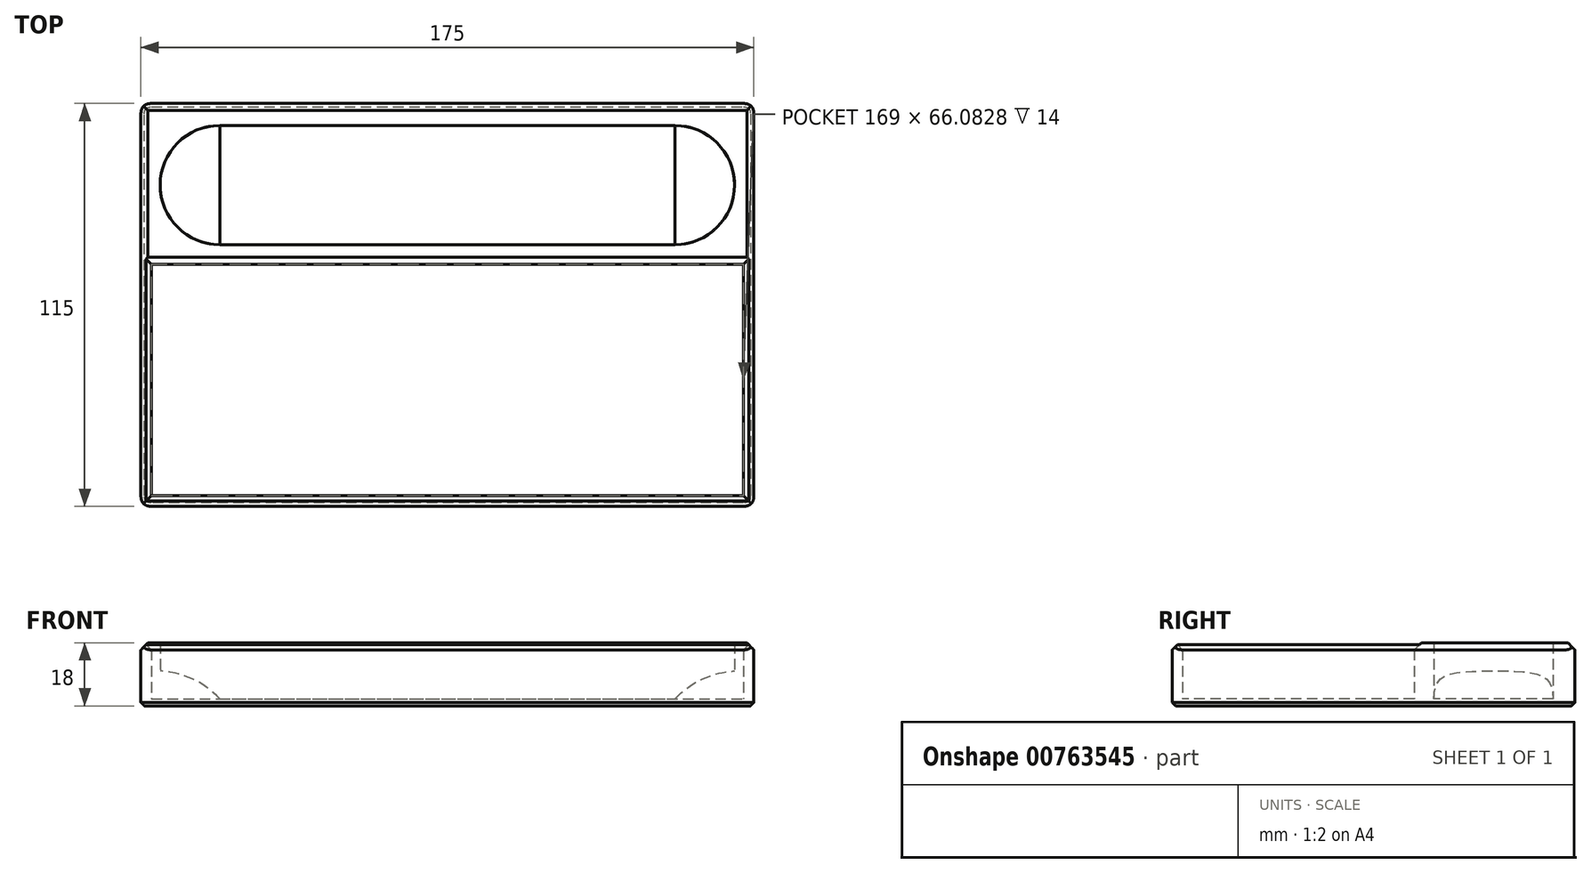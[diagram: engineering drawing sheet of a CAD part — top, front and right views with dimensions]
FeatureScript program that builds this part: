
annotation { "Feature Type Name" : "Feature", "Feature Type Description" : "" }
export const myFeature = defineFeature(function(context is Context, id is Id, definition is map)
    precondition{}
    {
        {
            var Q0;
            Q0=qCreatedBy(makeId("Top.planeOp"),FACE);
            var sketch = newSketch(context, id + "F0", { "sketchPlane" : qUnion([Q0])});
            skLineSegment(sketch, "E0.bottom", {"start": v(-100.46, 59.85) * mm, "end": v(74.54, 59.85) * mm});
            skLineSegment(sketch, "E0.top", {"start": v(-100.46, -55.15) * mm, "end": v(74.54, -55.15) * mm});
            skLineSegment(sketch, "E0.left", {"start": v(-100.46, 59.85) * mm, "end": v(-100.46, -55.15) * mm});
            skLineSegment(sketch, "E0.right", {"start": v(74.54, 59.85) * mm, "end": v(74.54, -55.15) * mm});
            skLineSegment(sketch, "E1.bottom", {"start": v(-77.96, 53.55) * mm, "end": v(52.04, 53.55) * mm});
            skLineSegment(sketch, "E1.top", {"start": v(-77.96, 19.55) * mm, "end": v(52.04, 19.55) * mm});
            skLineSegment(sketch, "E2.bottom", {"start": v(-97.46, 13.93) * mm, "end": v(71.54, 13.93) * mm});
            skLineSegment(sketch, "E2.top", {"start": v(-97.46, -52.15) * mm, "end": v(71.54, -52.15) * mm});
            skLineSegment(sketch, "E2.left", {"start": v(-97.46, 13.93) * mm, "end": v(-97.46, -52.15) * mm});
            skLineSegment(sketch, "E2.right", {"start": v(71.54, 13.93) * mm, "end": v(71.54, -52.15) * mm});
            skLineSegment(sketch, "E3", {"start": v(-97.46, -6.12) * mm, "end": v(-100.46, -6.12) * mm, "construction": true});
            skLineSegment(sketch, "E4", {"start": v(71.54, 0) * mm, "end": v(74.54, 0) * mm, "construction": true});
            skLineSegment(sketch, "E5", {"start": v(-2.83, -52.15) * mm, "end": v(-2.83, -55.15) * mm, "construction": true});
            skArc(sketch, "E6", {"start": v(-77.96, 53.55) * mm, "mid": v(-94.96, 36.55) * mm, "end": v(-77.96, 19.55) * mm});
            skPoint(sketch, "E6.third.point", {"position": v(-94.96, 36.55) * mm});
            skLineSegment(sketch, "E7", {"start": v(-94.96, 36.55) * mm, "end": v(-100.46, 36.55) * mm, "construction": true});
            skArc(sketch, "E8", {"start": v(52.04, 19.55) * mm, "mid": v(69.04, 36.55) * mm, "end": v(52.04, 53.55) * mm});
            skLineSegment(sketch, "E9", {"start": v(74.54, 36.55) * mm, "end": v(69.04, 36.55) * mm, "construction": true});
            skLineSegment(sketch, "E10", {"start": v(-77.96, 53.55) * mm, "end": v(-77.96, 19.55) * mm});
            skLineSegment(sketch, "E11", {"start": v(52.04, 53.55) * mm, "end": v(52.04, 19.55) * mm});
            skSolve(sketch);
        }
        {
            var Q0;
            Q0=makeQuery(id+"F0.imprint","IMPRINT",FACE,{"disambiguationData":[TD([[makeQuery(id+"F0.imprint","IMPRINT",EDGE,{"derivedFrom":sQuery(id+"F0.wireOp",EDGE,"E0.bottom")}),-1.0]])]});
            extrude(context, id + "F1", {"entities" : qUnion([Q0]), "depth" : 18 * mm, "offsetDistance" : 25 * mm});
        }
        {
            var Q0;
            Q0=makeQuery(id+"F0.imprint","IMPRINT",FACE,{"disambiguationData":[TD([[makeQuery(id+"F0.imprint","IMPRINT",EDGE,{"derivedFrom":sQuery(id+"F0.wireOp",EDGE,"E1.bottom")}),-1.0]])]});
            var Q1;
            Q1=makeQuery(id+"F0.imprint","IMPRINT",FACE,{"disambiguationData":[TD([[makeQuery(id+"F0.imprint","IMPRINT",EDGE,{"derivedFrom":sQuery(id+"F0.wireOp",EDGE,"E2.bottom")}),-1.0]])]});
            extrude(context, id + "F2", {"entities" : qUnion([Q0, Q1]), "operationType" : NewBodyOperationType.ADD, "depth" : 2 * mm, "offsetDistance" : 25 * mm});
        }
        {
            var Q0;
            Q0=makeQuery(id+"F0.imprint","IMPRINT",FACE,{"disambiguationData":[TD([[makeQuery(id+"F0.imprint","IMPRINT",EDGE,{"derivedFrom":sQuery(id+"F0.wireOp",EDGE,"E6")}),1.0]])]});
            var Q1;
            Q1=makeQuery(id+"F0.imprint","IMPRINT",FACE,{"disambiguationData":[TD([[makeQuery(id+"F0.imprint","IMPRINT",EDGE,{"derivedFrom":sQuery(id+"F0.wireOp",EDGE,"E8")}),1.0]])]});
            extrude(context, id + "F3", {"entities" : qUnion([Q0, Q1]), "operationType" : NewBodyOperationType.ADD, "depth" : 10 * mm, "offsetDistance" : 25 * mm});
        }
        {
            var Q0;
            Q0=makeQuery(id+"F3.opExtrude","CAP_EDGE",EDGE,{"disambiguationData":[OSD([sQuery(id+"F0.wireOp",EDGE,"E10")])],"isStart":false});
            var Q1;
            Q1=makeQuery(id+"F3.opExtrude","CAP_EDGE",EDGE,{"disambiguationData":[OSD([sQuery(id+"F0.wireOp",EDGE,"E11")])],"isStart":false});
            fillet(context, id + "F4", {"entities" : qUnion([Q0, Q1]), "radius" : 24.87 * mm, "tangentPropagation" : true, "allowEdgeOverflow" : false});
        }
        {
            var Q0;
            Q0=makeQuery(id+"F1.opExtrude","CAP_EDGE",EDGE,{"disambiguationData":[OSD([sQuery(id+"F0.wireOp",EDGE,"E2.bottom")])],"isStart":false});
            var Q1;
            Q1=makeQuery(id+"F1.opExtrude","CAP_EDGE",EDGE,{"disambiguationData":[OSD([sQuery(id+"F0.wireOp",EDGE,"E2.left")])],"isStart":false});
            var Q2;
            Q2=makeQuery(id+"F1.opExtrude","CAP_EDGE",EDGE,{"disambiguationData":[OSD([sQuery(id+"F0.wireOp",EDGE,"E2.top")])],"isStart":false});
            var Q3;
            Q3=makeQuery(id+"F1.opExtrude","CAP_EDGE",EDGE,{"disambiguationData":[OSD([sQuery(id+"F0.wireOp",EDGE,"E2.right")])],"isStart":false});
            var Q4;
            Q4=makeQuery(id+"F1.opExtrude","CAP_EDGE",EDGE,{"disambiguationData":[OSD([sQuery(id+"F0.wireOp",EDGE,"E0.left")])],"isStart":false});
            var Q5;
            Q5=makeQuery(id+"F1.opExtrude","CAP_EDGE",EDGE,{"disambiguationData":[OSD([sQuery(id+"F0.wireOp",EDGE,"E0.bottom")])],"isStart":false});
            var Q6;
            Q6=makeQuery(id+"F1.opExtrude","CAP_EDGE",EDGE,{"disambiguationData":[OSD([sQuery(id+"F0.wireOp",EDGE,"E0.right")])],"isStart":false});
            var Q7;
            Q7=makeQuery(id+"F1.opExtrude","CAP_EDGE",EDGE,{"disambiguationData":[OSD([sQuery(id+"F0.wireOp",EDGE,"E0.top")])],"isStart":false});
            chamfer(context, id + "F5", {"entities" : qUnion([Q0, Q1, Q2, Q3, Q4, Q5, Q6, Q7]), "width" : 2 * mm, "tangentPropagation" : true});
        }
        {
            var Q0;
            Q0=makeQuery(id+"F1.opExtrude","SWEPT_EDGE",EDGE,{"disambiguationData":[OSD([sQuery(id+"F0.wireOp",EDGE,"E0.top"),sQuery(id+"F0.wireOp",EDGE,"E0.right")])]});
            var Q1;
            Q1=makeQuery(id+"F1.opExtrude","SWEPT_EDGE",EDGE,{"disambiguationData":[OSD([sQuery(id+"F0.wireOp",EDGE,"E0.bottom"),sQuery(id+"F0.wireOp",EDGE,"E0.right")])]});
            var Q2;
            Q2=makeQuery(id+"F1.opExtrude","SWEPT_EDGE",EDGE,{"disambiguationData":[OSD([sQuery(id+"F0.wireOp",EDGE,"E0.top"),sQuery(id+"F0.wireOp",EDGE,"E0.left")])]});
            var Q3;
            Q3=makeQuery(id+"F1.opExtrude","SWEPT_EDGE",EDGE,{"disambiguationData":[OSD([sQuery(id+"F0.wireOp",EDGE,"E0.bottom"),sQuery(id+"F0.wireOp",EDGE,"E0.left")])]});
            fillet(context, id + "F6", {"entities" : qUnion([Q0, Q1, Q2, Q3]), "radius" : 3 * mm, "tangentPropagation" : true, "rho" : 0.5, "crossSection" : FilletCrossSection.CONIC, "allowEdgeOverflow" : false});
        }
        {
            var Q0;
            Q0=makeQuery(id+"F1.opExtrude","CAP_EDGE",EDGE,{"disambiguationData":[OSD([sQuery(id+"F0.wireOp",EDGE,"E0.top")])],"isStart":true});
            var Q1;
            {var subQ0=sQuery(id+"F0.wireOp",EDGE,"E11");var subQ1=sQuery(id+"F0.wireOp",EDGE,"E8");var subQ2=sQuery(id+"F0.wireOp",EDGE,"E10");var subQ3=sQuery(id+"F0.wireOp",EDGE,"E6");var subQ4=sQuery(id+"F0.wireOp",EDGE,"E2.right");var subQ5=sQuery(id+"F0.wireOp",EDGE,"E2.left");var subQ6=sQuery(id+"F0.wireOp",EDGE,"E2.top");var subQ7=sQuery(id+"F0.wireOp",EDGE,"E2.bottom");var subQ8=sQuery(id+"F0.wireOp",EDGE,"E1.top");var subQ9=sQuery(id+"F0.wireOp",EDGE,"E1.bottom");var subQ10=sQuery(id+"F0.wireOp",EDGE,"E0.right");var subQ11=sQuery(id+"F0.wireOp",EDGE,"E0.top");Q1=makeQuery(id+"F6.opFillet","BLEND_EDGE",EDGE,{"blendedFrom":[makeQuery(id+"F1.opExtrude","SWEPT_EDGE",EDGE,{"disambiguationData":[OSD([subQ11,subQ10])]}),makeQuery(id+"F3.boolean.opBoolean","MERGE",FACE,{"derivedFrom":[makeQuery(id+"F2.boolean.opBoolean","MERGE",FACE,{"derivedFrom":[makeQuery(id+"F1.opExtrude","CAP_FACE",FACE,{"disambiguationData":[OSD([sQuery(id+"F0.wireOp",EDGE,"E0.bottom"),subQ11,sQuery(id+"F0.wireOp",EDGE,"E0.left"),subQ10,subQ9,subQ8,subQ7,subQ6,subQ5,subQ4,subQ3,subQ1])],"isStart":true}),makeQuery(id+"F2.opExtrude","CAP_FACE",FACE,{"disambiguationData":[OSD([subQ9,subQ8,subQ2,subQ0])],"isStart":true}),makeQuery(id+"F2.opExtrude","CAP_FACE",FACE,{"disambiguationData":[OSD([subQ7,subQ6,subQ5,subQ4])],"isStart":true})]}),makeQuery(id+"F3.opExtrude","CAP_FACE",FACE,{"disambiguationData":[OSD([subQ3,subQ2])],"isStart":true}),makeQuery(id+"F3.opExtrude","CAP_FACE",FACE,{"disambiguationData":[OSD([subQ1,subQ0])],"isStart":true})]})],"blendedInto":[makeQuery(id+"F3.boolean.opBoolean","MERGE",FACE,{"derivedFrom":[makeQuery(id+"F2.boolean.opBoolean","MERGE",FACE,{"derivedFrom":[makeQuery(id+"F1.opExtrude","CAP_FACE",FACE,{"disambiguationData":[OSD([sQuery(id+"F0.wireOp",EDGE,"E0.bottom"),subQ11,sQuery(id+"F0.wireOp",EDGE,"E0.left"),subQ10,subQ9,subQ8,subQ7,subQ6,subQ5,subQ4,subQ3,subQ1])],"isStart":true}),makeQuery(id+"F2.opExtrude","CAP_FACE",FACE,{"disambiguationData":[OSD([subQ9,subQ8,subQ2,subQ0])],"isStart":true}),makeQuery(id+"F2.opExtrude","CAP_FACE",FACE,{"disambiguationData":[OSD([subQ7,subQ6,subQ5,subQ4])],"isStart":true})]}),makeQuery(id+"F3.opExtrude","CAP_FACE",FACE,{"disambiguationData":[OSD([subQ3,subQ2])],"isStart":true}),makeQuery(id+"F3.opExtrude","CAP_FACE",FACE,{"disambiguationData":[OSD([subQ1,subQ0])],"isStart":true})]})]});}
            chamfer(context, id + "F7", {"entities" : qUnion([Q0, Q1]), "width" : 1 * mm, "tangentPropagation" : true});
        }
    });
